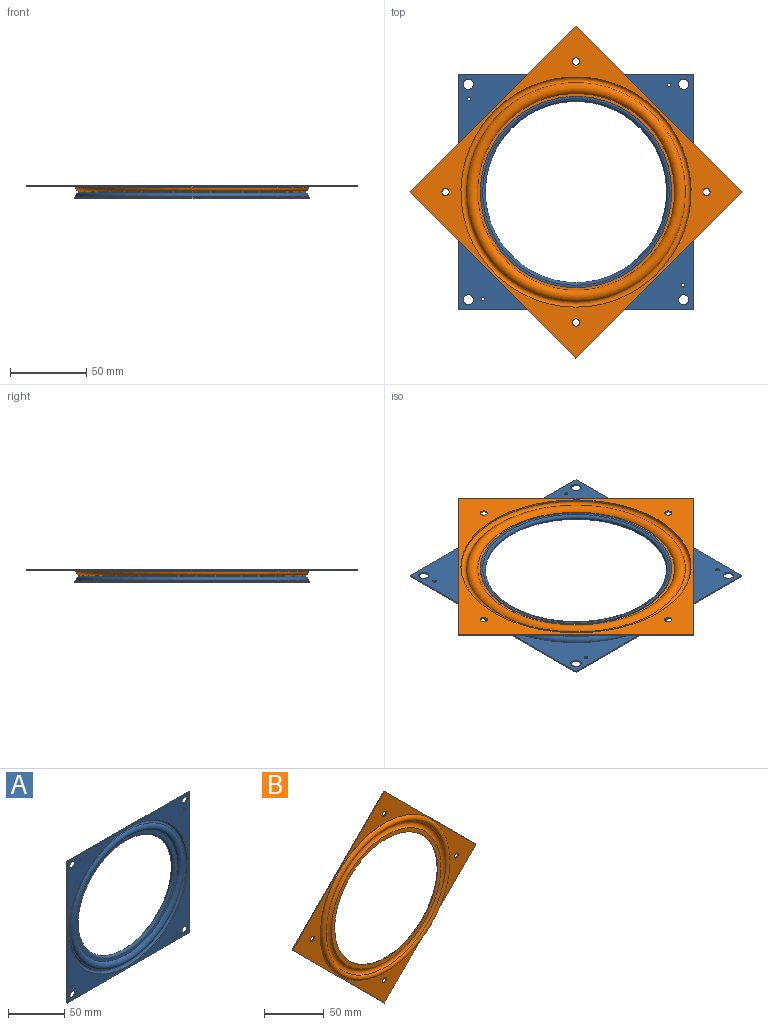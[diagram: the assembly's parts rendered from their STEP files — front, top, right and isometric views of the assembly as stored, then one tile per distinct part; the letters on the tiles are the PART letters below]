
ASSEMBLY  parts=2 mates=1
PART A: 27 faces, bbox 165.1x6.6x165.1 mm
  f0: torus R=61.21mm, axis (0,1,0), area 1244.7mm2, adj f19,f20
  f1: cylinder r=1.19mm len=2.38mm, axis (0,1,0), area 5.5mm2, adj f17,f18
  f2: cylinder r=1.19mm len=2.38mm, axis (0,1,0), area 5.5mm2, adj f17,f18
  f3: cylinder r=1.19mm len=2.38mm, axis (0,1,0), area 5.5mm2, adj f17,f18
  f4: cylinder r=1.19mm len=2.38mm, axis (0,1,0), area 5.5mm2, adj f17,f18
  f5: cylinder r=3.38mm len=6.76mm, axis (0,1,0), area 15.6mm2, adj f17,f18
  f6: cylinder r=3.38mm len=6.76mm, axis (0,1,0), area 15.6mm2, adj f17,f18
  f7: cylinder r=3.38mm len=6.76mm, axis (0,1,0), area 15.6mm2, adj f17,f18
  f8: cylinder r=3.38mm len=6.76mm, axis (0,1,0), area 15.6mm2, adj f17,f18
  f9: cylinder r=75.53mm len=151.06mm, axis (0,1,0), area 482.2mm2, adj f10,f17
  f10: torus R=73.5mm, axis (0,1,0), area 2469.6mm2, adj f9,f11
  f11: torus R=68.22mm, axis (0,1,0), area 4094.3mm2, adj f10,f22
  f12: torus R=61.21mm, axis (0,1,0), area 2108.7mm2, adj f21,f22
  f13: cylinder r=62.75mm len=125.5mm, axis (0,1,0), area 290.4mm2, adj f20,f21
  f14: torus R=68.22mm, axis (0,1,0), area 3585mm2, adj f15,f19
  f15: torus R=73.5mm, axis (0,1,0), area 3371.3mm2, adj f14,f16
  f16: cylinder r=76.27mm len=152.53mm, axis (0,1,0), area 133.9mm2, adj f15,f18
  f17: plane 154x154mm, normal (0,-1,0), area 5633.1mm2, adj f1,f2,f3,f4,f5,f6,f7,f8
  f18: plane 154x154mm, normal (0,1,0), area 5281.8mm2, adj f1,f2,f3,f4,f5,f6,f7,f8
  f19: plane 129.81x129.81mm, normal (0,1,0), area 1461.4mm2, adj f0,f14
  f20: plane 125.5x125.5mm, normal (0,-1,0), area 597.6mm2, adj f0,f13
  f21: plane 125.5x125.5mm, normal (0,1,0), area 597.6mm2, adj f12,f13
  f22: plane 128.57x128.57mm, normal (0,-1,0), area 1210mm2, adj f11,f12
  f23: plane 154x0.74mm, normal (0,0,-1), area 113.4mm2, adj f17,f18,f24,f26
  f24: plane 154x0.74mm, normal (-1,0,0), area 113.4mm2, adj f17,f18,f23,f25
  f25: plane 154x0.74mm, normal (0,0,1), area 113.4mm2, adj f17,f18,f24,f26
  f26: plane 154x0.74mm, normal (1,0,0), area 113.4mm2, adj f17,f18,f23,f25
PART B: 19 faces, bbox 217.8x5x217.8 mm
  f0: cylinder r=2.39mm len=4.78mm, axis (0,1,0), area 11.1mm2, adj f11,f12
  f1: cylinder r=2.39mm len=4.78mm, axis (0,1,0), area 11.1mm2, adj f11,f12
  f2: cylinder r=2.39mm len=4.78mm, axis (0,1,0), area 11.1mm2, adj f11,f12
  f3: cylinder r=2.39mm len=4.78mm, axis (0,1,0), area 11.1mm2, adj f11,f12
  f4: cylinder r=76.27mm len=152.53mm, axis (0,1,0), area 133.9mm2, adj f5,f11
  f5: torus R=73.5mm, axis (0,1,0), area 3371.3mm2, adj f4,f6
  f6: torus R=68.22mm, axis (0,1,0), area 3255.9mm2, adj f5,f14
  f7: cylinder r=61.21mm len=122.43mm, axis (0,1,0), area 283.3mm2, adj f13,f14
  f8: torus R=68.22mm, axis (0,1,0), area 3753.6mm2, adj f9,f13
  f9: torus R=73.5mm, axis (0,1,0), area 2469.6mm2, adj f8,f10
  f10: cylinder r=75.53mm len=151.06mm, axis (0,1,0), area 482.2mm2, adj f9,f12
  f11: plane 217.79x217.79mm, normal (0,-1,0), area 5371.4mm2, adj f0,f1,f2,f3,f4,f15,f16,f17
  f12: plane 217.79x217.79mm, normal (0,1,0), area 5722.6mm2, adj f0,f1,f2,f3,f10,f15,f16,f17
  f13: plane 129.15x129.15mm, normal (0,1,0), area 1328.6mm2, adj f7,f8
  f14: plane 130.13x130.13mm, normal (0,-1,0), area 1528.3mm2, adj f6,f7
  f15: plane 108.89x108.89mm, normal (-0.71,0,-0.71), area 113.4mm2, adj f11,f12,f16,f18
  f16: plane 108.89x108.89mm, normal (-0.71,0,0.71), area 113.4mm2, adj f11,f12,f15,f17
  f17: plane 108.89x108.89mm, normal (0.71,0,0.71), area 113.4mm2, adj f11,f12,f16,f18
  f18: plane 108.89x108.89mm, normal (0.71,0,-0.71), area 113.4mm2, adj f11,f12,f15,f17
PLACE A rot(axis=(1,0,0),90deg) t=(0,0,-3.3)mm
PLACE B rot(axis=(1,0,0),90deg) t=(0,0,-3.3)mm
MATE revolute A.f0 <-> B.f4  axis (0,0,-1) through (0,0,-2.26)mm
